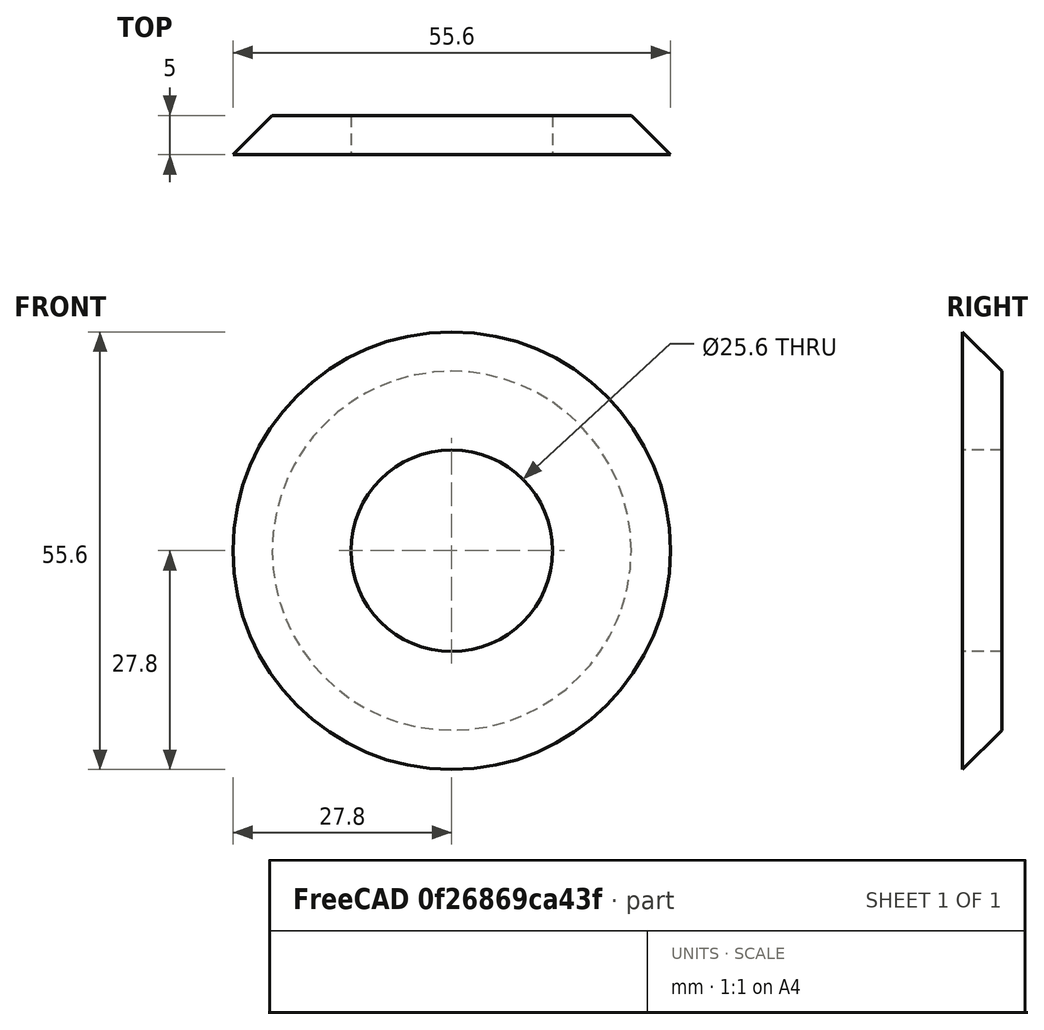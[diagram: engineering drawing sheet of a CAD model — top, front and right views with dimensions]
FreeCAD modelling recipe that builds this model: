
FCSTD DOCUMENT  (FreeCAD 0.19R24276 (Git))
Label: Tension_roller_v4_out_part
License: All rights reserved
LicenseURL: http://en.wikipedia.org/wiki/All_rights_reserved
objects: Sketcher::SketchObject×1, PartDesign::Revolution×1, PartDesign::Body×1
note: 4 computed .brp shape members not serialized (recipe doc carries the construction recipe); baked Part::Feature solids carry a one-line shape summary decoded from their .brp

FEATURE [Sketcher::SketchObject] Sketch
  FullyConstrained = true
  MapMode = 5
  Support = -> [XY_Plane]
  sketch-geometry (4):
    g0: LineSegment StartX=27.8 StartY=0 StartZ=0 EndX=22.8 EndY=5 EndZ=0
    g1: LineSegment StartX=22.8 StartY=5 StartZ=0 EndX=12.8 EndY=5 EndZ=0
    g2: LineSegment StartX=12.8 StartY=5 StartZ=0 EndX=12.8 EndY=0 EndZ=0
    g3: LineSegment StartX=12.8 StartY=0 StartZ=0 EndX=27.8 EndY=0 EndZ=0
  constraints (12):
    c: PointOnObject(g0,g-1)
    c: Horizontal(g1)
    c: Coincident(g2,g1)
    c: PointOnObject(g2,g-1)
    c: Coincident(g3,g2)
    c: Coincident(g3,g0)
    c: Vertical(g2)
    c: Coincident(g0,g1)
    c: DistanceX(g-1,g2) = 12.8
    c: DistanceX(g1,g1) = 10
    c: DistanceY(g2,g2) = 5
    c: Angle(g1,g0) = 2.35619
FEATURE [PartDesign::Revolution] Revolution
  Angle = 360
  Axis = (0,1,0)
  Base = (0,0,0)
  Profile = -> Sketch
  ReferenceAxis = -> Sketch [V_Axis]
  Reversed = true
FEATURE [PartDesign::Body] Body
  Group = -> [Sketch,Revolution]
  Origin = -> Origin
  Tip = -> Revolution
